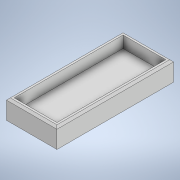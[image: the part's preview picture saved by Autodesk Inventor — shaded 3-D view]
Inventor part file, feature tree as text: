
AUTODESK INVENTOR PART (.ipt)
format: ipt  version: 2021 (Build 250183000, 183)  size: 120,320 bytes
history: native  units: in
note: dims shown in document units (in); Inventor stores cm internally (conversion verified against a paired STEP export)
features: extrude x2, sketch x2, chamfer x1, projected_geometry x1
ambient origin geometry x8: Origin, YZ Plane, XZ Plane, XY Plane, X Axis, Y Axis, Z Axis, Center Point
bodies: Solid1 (feature_tree)
feature tree (6):
  extrude  "Extrusion1"  Depth=0.5118in
  extrude  "Extrusion2"  Depth=0.1181in TaperAngle=0.0deg
  chamfer  "Chamfer1"  Distance=0.0787in Angle=45.0deg
  sketch  "Sketch1"  dims[d0=1.1811in d1=0.5118in]
  sketch  "Sketch2"  dims[d2=0.0787in d3=0.0in d8=0.1181in d9=0.0in d10=0.0197in d11=0.0787in d12=45.0deg d13=0.0394in d14=0.0394in d15=0.4331in d16=1.1024in]
  projected_geometry  "Projected Loop1"
